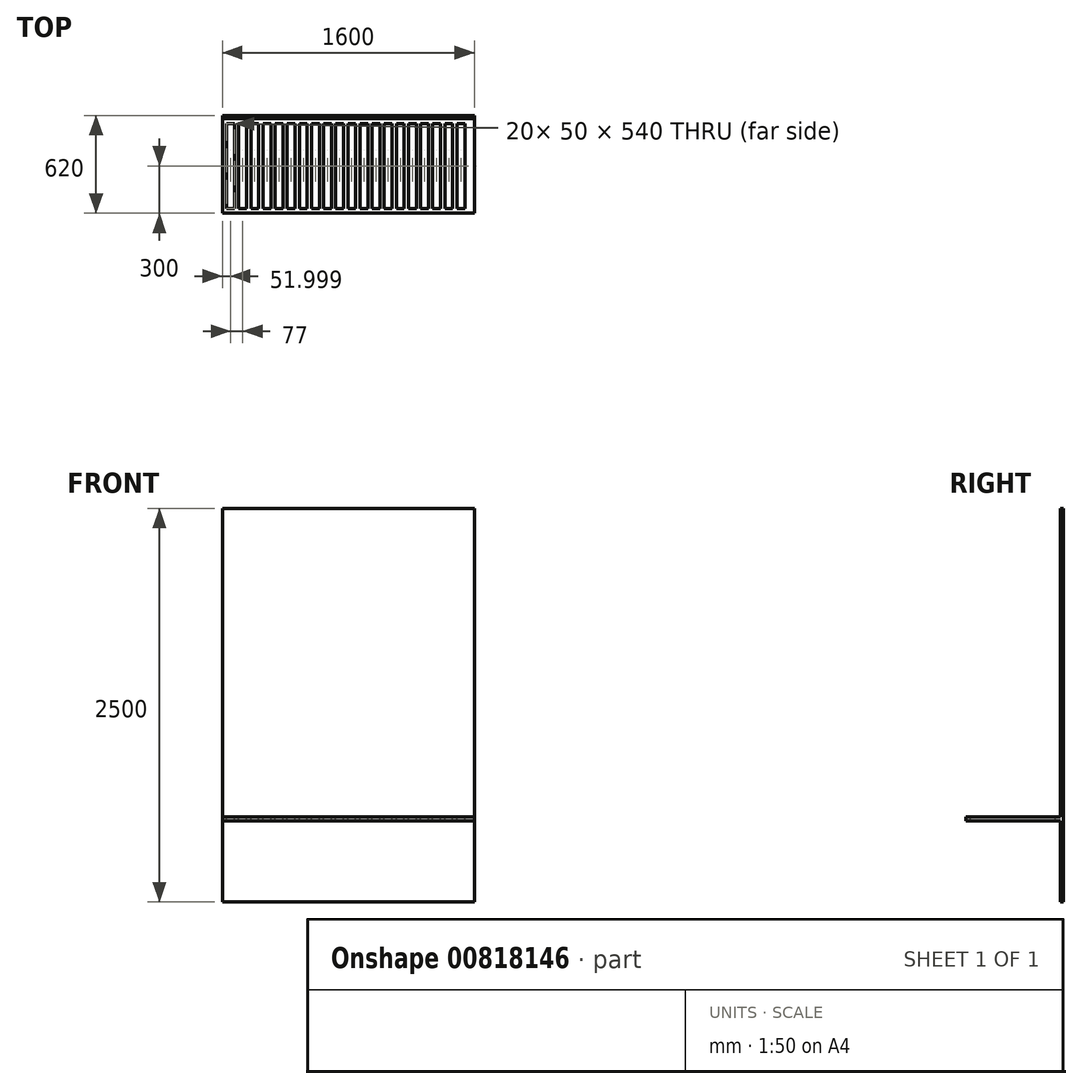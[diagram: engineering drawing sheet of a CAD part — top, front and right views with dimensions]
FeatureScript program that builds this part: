
annotation { "Feature Type Name" : "Feature", "Feature Type Description" : "" }
export const myFeature = defineFeature(function(context is Context, id is Id, definition is map)
    precondition{}
    {
        {
            var Q0;
            Q0=qCreatedBy(makeId("Front.planeOp"),FACE);
            var sketch = newSketch(context, id + "F0", { "sketchPlane" : qUnion([Q0])});
            skLineSegment(sketch, "E0.bottom", {"start": v(-816.96, 1960.36) * mm, "end": v(783.04, 1960.36) * mm});
            skLineSegment(sketch, "E0.top", {"start": v(-816.96, -539.64) * mm, "end": v(783.04, -539.64) * mm});
            skLineSegment(sketch, "E0.left", {"start": v(-816.96, 1960.36) * mm, "end": v(-816.96, -539.64) * mm});
            skLineSegment(sketch, "E0.right", {"start": v(783.04, 1960.36) * mm, "end": v(783.04, -539.64) * mm});
            skSolve(sketch);
        }
        {
            var Q0;
            Q0=makeQuery(id+"F0.imprint","IMPRINT",FACE,{"disambiguationData":[TD([[makeQuery(id+"F0.imprint","IMPRINT",EDGE,{"derivedFrom":sQuery(id+"F0.wireOp",EDGE,"E0.bottom")}),-1.0]])]});
            extrude(context, id + "F1", {"entities" : qUnion([Q0]), "depth" : 20 * mm, "offsetDistance" : 25 * mm});
        }
        {
            var Q0;
            Q0=makeQuery(id+"F1.opExtrude","CAP_FACE",FACE,{"disambiguationData":[OSD([sQuery(id+"F0.wireOp",EDGE,"E0.bottom"),sQuery(id+"F0.wireOp",EDGE,"E0.top"),sQuery(id+"F0.wireOp",EDGE,"E0.left"),sQuery(id+"F0.wireOp",EDGE,"E0.right")])],"isStart":false});
            var sketch = newSketch(context, id + "F2", { "sketchPlane" : qUnion([Q0])});
            skLineSegment(sketch, "E1.bottom", {"start": v(783.04, -25) * mm, "end": v(-816.96, -25) * mm});
            skLineSegment(sketch, "E1.top", {"start": v(783.04, 0) * mm, "end": v(-816.96, 0) * mm});
            skLineSegment(sketch, "E1.left", {"start": v(783.04, -25) * mm, "end": v(783.04, 0) * mm});
            skLineSegment(sketch, "E1.right", {"start": v(-816.96, -25) * mm, "end": v(-816.96, 0) * mm});
            skSolve(sketch);
        }
        {
            var Q0;
            Q0=makeQuery(id+"F2.imprint","IMPRINT",FACE,{"disambiguationData":[TD([[makeQuery(id+"F2.imprint","IMPRINT",EDGE,{"derivedFrom":sQuery(id+"F2.wireOp",EDGE,"E1.bottom")}),-1.0]])]});
            extrude(context, id + "F3", {"entities" : qUnion([Q0]), "operationType" : NewBodyOperationType.ADD, "depth" : 600 * mm, "offsetDistance" : 25 * mm});
        }
        {
            var Q0;
            Q0=makeQuery(id+"F3.opExtrude","SWEPT_FACE",FACE,{"disambiguationData":[OSD([sQuery(id+"F2.wireOp",EDGE,"E1.top")])]});
            var sketch = newSketch(context, id + "F4", { "sketchPlane" : qUnion([Q0])});
            skLineSegment(sketch, "E2.bottom", {"start": v(723.04, -590) * mm, "end": v(673.04, -590) * mm});
            skLineSegment(sketch, "E2.top", {"start": v(723.04, -50) * mm, "end": v(673.04, -50) * mm});
            skLineSegment(sketch, "E2.left", {"start": v(723.04, -590) * mm, "end": v(723.04, -50) * mm});
            skLineSegment(sketch, "E2.right", {"start": v(673.04, -590) * mm, "end": v(673.04, -50) * mm});
            skLineSegment(sketch, "E3.1.0.0", {"start": v(646.04, -50) * mm, "end": v(596.04, -50) * mm});
            skLineSegment(sketch, "E3.1.0.1", {"start": v(646.04, -590) * mm, "end": v(646.04, -50) * mm});
            skLineSegment(sketch, "E3.1.0.2", {"start": v(596.04, -590) * mm, "end": v(596.04, -50) * mm});
            skLineSegment(sketch, "E3.1.0.3", {"start": v(646.04, -590) * mm, "end": v(596.04, -590) * mm});
            skLineSegment(sketch, "E3.2.0.0", {"start": v(569.04, -50) * mm, "end": v(519.04, -50) * mm});
            skLineSegment(sketch, "E3.2.0.1", {"start": v(569.04, -590) * mm, "end": v(569.04, -50) * mm});
            skLineSegment(sketch, "E3.2.0.2", {"start": v(519.04, -590) * mm, "end": v(519.04, -50) * mm});
            skLineSegment(sketch, "E3.2.0.3", {"start": v(569.04, -590) * mm, "end": v(519.04, -590) * mm});
            skLineSegment(sketch, "E3.3.0.0", {"start": v(492.04, -50) * mm, "end": v(442.04, -50) * mm});
            skLineSegment(sketch, "E3.3.0.1", {"start": v(492.04, -590) * mm, "end": v(492.04, -50) * mm});
            skLineSegment(sketch, "E3.3.0.2", {"start": v(442.04, -590) * mm, "end": v(442.04, -50) * mm});
            skLineSegment(sketch, "E3.3.0.3", {"start": v(492.04, -590) * mm, "end": v(442.04, -590) * mm});
            skLineSegment(sketch, "E3.4.0.0", {"start": v(415.04, -50) * mm, "end": v(365.04, -50) * mm});
            skLineSegment(sketch, "E3.4.0.1", {"start": v(415.04, -590) * mm, "end": v(415.04, -50) * mm});
            skLineSegment(sketch, "E3.4.0.2", {"start": v(365.04, -590) * mm, "end": v(365.04, -50) * mm});
            skLineSegment(sketch, "E3.4.0.3", {"start": v(415.04, -590) * mm, "end": v(365.04, -590) * mm});
            skLineSegment(sketch, "E3.5.0.0", {"start": v(338.04, -50) * mm, "end": v(288.04, -50) * mm});
            skLineSegment(sketch, "E3.5.0.1", {"start": v(338.04, -590) * mm, "end": v(338.04, -50) * mm});
            skLineSegment(sketch, "E3.5.0.2", {"start": v(288.04, -590) * mm, "end": v(288.04, -50) * mm});
            skLineSegment(sketch, "E3.5.0.3", {"start": v(338.04, -590) * mm, "end": v(288.04, -590) * mm});
            skLineSegment(sketch, "E3.6.0.0", {"start": v(261.04, -50) * mm, "end": v(211.04, -50) * mm});
            skLineSegment(sketch, "E3.6.0.1", {"start": v(261.04, -590) * mm, "end": v(261.04, -50) * mm});
            skLineSegment(sketch, "E3.6.0.2", {"start": v(211.04, -590) * mm, "end": v(211.04, -50) * mm});
            skLineSegment(sketch, "E3.6.0.3", {"start": v(261.04, -590) * mm, "end": v(211.04, -590) * mm});
            skLineSegment(sketch, "E3.7.0.0", {"start": v(184.04, -50) * mm, "end": v(134.04, -50) * mm});
            skLineSegment(sketch, "E3.7.0.1", {"start": v(184.04, -590) * mm, "end": v(184.04, -50) * mm});
            skLineSegment(sketch, "E3.7.0.2", {"start": v(134.04, -590) * mm, "end": v(134.04, -50) * mm});
            skLineSegment(sketch, "E3.7.0.3", {"start": v(184.04, -590) * mm, "end": v(134.04, -590) * mm});
            skLineSegment(sketch, "E3.8.0.0", {"start": v(107.04, -50) * mm, "end": v(57.04, -50) * mm});
            skLineSegment(sketch, "E3.8.0.1", {"start": v(107.04, -590) * mm, "end": v(107.04, -50) * mm});
            skLineSegment(sketch, "E3.8.0.2", {"start": v(57.04, -590) * mm, "end": v(57.04, -50) * mm});
            skLineSegment(sketch, "E3.8.0.3", {"start": v(107.04, -590) * mm, "end": v(57.04, -590) * mm});
            skLineSegment(sketch, "E3.9.0.0", {"start": v(30.04, -50) * mm, "end": v(-19.96, -50) * mm});
            skLineSegment(sketch, "E3.9.0.1", {"start": v(30.04, -590) * mm, "end": v(30.04, -50) * mm});
            skLineSegment(sketch, "E3.9.0.2", {"start": v(-19.96, -590) * mm, "end": v(-19.96, -50) * mm});
            skLineSegment(sketch, "E3.9.0.3", {"start": v(30.04, -590) * mm, "end": v(-19.96, -590) * mm});
            skLineSegment(sketch, "E3.10.0.0", {"start": v(-46.96, -50) * mm, "end": v(-96.96, -50) * mm});
            skLineSegment(sketch, "E3.10.0.1", {"start": v(-46.96, -590) * mm, "end": v(-46.96, -50) * mm});
            skLineSegment(sketch, "E3.10.0.2", {"start": v(-96.96, -590) * mm, "end": v(-96.96, -50) * mm});
            skLineSegment(sketch, "E3.10.0.3", {"start": v(-46.96, -590) * mm, "end": v(-96.96, -590) * mm});
            skLineSegment(sketch, "E3.11.0.0", {"start": v(-123.96, -50) * mm, "end": v(-173.96, -50) * mm});
            skLineSegment(sketch, "E3.11.0.1", {"start": v(-123.96, -590) * mm, "end": v(-123.96, -50) * mm});
            skLineSegment(sketch, "E3.11.0.2", {"start": v(-173.96, -590) * mm, "end": v(-173.96, -50) * mm});
            skLineSegment(sketch, "E3.11.0.3", {"start": v(-123.96, -590) * mm, "end": v(-173.96, -590) * mm});
            skLineSegment(sketch, "E3.12.0.0", {"start": v(-200.96, -50) * mm, "end": v(-250.96, -50) * mm});
            skLineSegment(sketch, "E3.12.0.1", {"start": v(-200.96, -590) * mm, "end": v(-200.96, -50) * mm});
            skLineSegment(sketch, "E3.12.0.2", {"start": v(-250.96, -590) * mm, "end": v(-250.96, -50) * mm});
            skLineSegment(sketch, "E3.12.0.3", {"start": v(-200.96, -590) * mm, "end": v(-250.96, -590) * mm});
            skLineSegment(sketch, "E3.13.0.0", {"start": v(-277.96, -50) * mm, "end": v(-327.96, -50) * mm});
            skLineSegment(sketch, "E3.13.0.1", {"start": v(-277.96, -590) * mm, "end": v(-277.96, -50) * mm});
            skLineSegment(sketch, "E3.13.0.2", {"start": v(-327.96, -590) * mm, "end": v(-327.96, -50) * mm});
            skLineSegment(sketch, "E3.13.0.3", {"start": v(-277.96, -590) * mm, "end": v(-327.96, -590) * mm});
            skLineSegment(sketch, "E3.14.0.0", {"start": v(-354.96, -50) * mm, "end": v(-404.96, -50) * mm});
            skLineSegment(sketch, "E3.14.0.1", {"start": v(-354.96, -590) * mm, "end": v(-354.96, -50) * mm});
            skLineSegment(sketch, "E3.14.0.2", {"start": v(-404.96, -590) * mm, "end": v(-404.96, -50) * mm});
            skLineSegment(sketch, "E3.14.0.3", {"start": v(-354.96, -590) * mm, "end": v(-404.96, -590) * mm});
            skLineSegment(sketch, "E3.15.0.0", {"start": v(-431.96, -50) * mm, "end": v(-481.96, -50) * mm});
            skLineSegment(sketch, "E3.15.0.1", {"start": v(-431.96, -590) * mm, "end": v(-431.96, -50) * mm});
            skLineSegment(sketch, "E3.15.0.2", {"start": v(-481.96, -590) * mm, "end": v(-481.96, -50) * mm});
            skLineSegment(sketch, "E3.15.0.3", {"start": v(-431.96, -590) * mm, "end": v(-481.96, -590) * mm});
            skLineSegment(sketch, "E3.16.0.0", {"start": v(-508.96, -50) * mm, "end": v(-558.96, -50) * mm});
            skLineSegment(sketch, "E3.16.0.1", {"start": v(-508.96, -590) * mm, "end": v(-508.96, -50) * mm});
            skLineSegment(sketch, "E3.16.0.2", {"start": v(-558.96, -590) * mm, "end": v(-558.96, -50) * mm});
            skLineSegment(sketch, "E3.16.0.3", {"start": v(-508.96, -590) * mm, "end": v(-558.96, -590) * mm});
            skLineSegment(sketch, "E3.17.0.0", {"start": v(-585.96, -50) * mm, "end": v(-635.96, -50) * mm});
            skLineSegment(sketch, "E3.17.0.1", {"start": v(-585.96, -590) * mm, "end": v(-585.96, -50) * mm});
            skLineSegment(sketch, "E3.17.0.2", {"start": v(-635.96, -590) * mm, "end": v(-635.96, -50) * mm});
            skLineSegment(sketch, "E3.17.0.3", {"start": v(-585.96, -590) * mm, "end": v(-635.96, -590) * mm});
            skLineSegment(sketch, "E3.18.0.0", {"start": v(-662.96, -50) * mm, "end": v(-712.96, -50) * mm});
            skLineSegment(sketch, "E3.18.0.1", {"start": v(-662.96, -590) * mm, "end": v(-662.96, -50) * mm});
            skLineSegment(sketch, "E3.18.0.2", {"start": v(-712.96, -590) * mm, "end": v(-712.96, -50) * mm});
            skLineSegment(sketch, "E3.18.0.3", {"start": v(-662.96, -590) * mm, "end": v(-712.96, -590) * mm});
            skLineSegment(sketch, "E3.19.0.0", {"start": v(-739.96, -50) * mm, "end": v(-789.96, -50) * mm});
            skLineSegment(sketch, "E3.19.0.1", {"start": v(-739.96, -590) * mm, "end": v(-739.96, -50) * mm});
            skLineSegment(sketch, "E3.19.0.2", {"start": v(-789.96, -590) * mm, "end": v(-789.96, -50) * mm});
            skLineSegment(sketch, "E3.19.0.3", {"start": v(-739.96, -590) * mm, "end": v(-789.96, -590) * mm});
            skLineSegment(sketch, "E3.direction1", {"start": v(673.04, -590) * mm, "end": v(596.04, -590) * mm, "construction": true});
            skSolve(sketch);
        }
        {
            var Q0;
            Q0=makeQuery(id+"F4.imprint","IMPRINT",FACE,{"disambiguationData":[TD([[makeQuery(id+"F4.imprint","IMPRINT",EDGE,{"derivedFrom":sQuery(id+"F4.wireOp",EDGE,"E3.16.0.0")}),1.0]])]});
            var Q1;
            Q1=makeQuery(id+"F4.imprint","IMPRINT",FACE,{"disambiguationData":[TD([[makeQuery(id+"F4.imprint","IMPRINT",EDGE,{"derivedFrom":sQuery(id+"F4.wireOp",EDGE,"E3.17.0.0")}),1.0]])]});
            var Q2;
            Q2=makeQuery(id+"F4.imprint","IMPRINT",FACE,{"disambiguationData":[TD([[makeQuery(id+"F4.imprint","IMPRINT",EDGE,{"derivedFrom":sQuery(id+"F4.wireOp",EDGE,"E3.18.0.0")}),1.0]])]});
            var Q3;
            Q3=makeQuery(id+"F4.imprint","IMPRINT",FACE,{"disambiguationData":[TD([[makeQuery(id+"F4.imprint","IMPRINT",EDGE,{"derivedFrom":sQuery(id+"F4.wireOp",EDGE,"E3.19.0.0")}),1.0]])]});
            var Q4;
            Q4=makeQuery(id+"F4.imprint","IMPRINT",FACE,{"disambiguationData":[TD([[makeQuery(id+"F4.imprint","IMPRINT",EDGE,{"derivedFrom":sQuery(id+"F4.wireOp",EDGE,"E3.15.0.0")}),1.0]])]});
            var Q5;
            Q5=makeQuery(id+"F4.imprint","IMPRINT",FACE,{"disambiguationData":[TD([[makeQuery(id+"F4.imprint","IMPRINT",EDGE,{"derivedFrom":sQuery(id+"F4.wireOp",EDGE,"E3.13.0.0")}),1.0]])]});
            var Q6;
            Q6=makeQuery(id+"F4.imprint","IMPRINT",FACE,{"disambiguationData":[TD([[makeQuery(id+"F4.imprint","IMPRINT",EDGE,{"derivedFrom":sQuery(id+"F4.wireOp",EDGE,"E3.14.0.0")}),1.0]])]});
            var Q7;
            Q7=makeQuery(id+"F4.imprint","IMPRINT",FACE,{"disambiguationData":[TD([[makeQuery(id+"F4.imprint","IMPRINT",EDGE,{"derivedFrom":sQuery(id+"F4.wireOp",EDGE,"E2.bottom")}),-1.0]])]});
            var Q8;
            Q8=makeQuery(id+"F4.imprint","IMPRINT",FACE,{"disambiguationData":[TD([[makeQuery(id+"F4.imprint","IMPRINT",EDGE,{"derivedFrom":sQuery(id+"F4.wireOp",EDGE,"E3.1.0.0")}),1.0]])]});
            var Q9;
            Q9=makeQuery(id+"F4.imprint","IMPRINT",FACE,{"disambiguationData":[TD([[makeQuery(id+"F4.imprint","IMPRINT",EDGE,{"derivedFrom":sQuery(id+"F4.wireOp",EDGE,"E3.2.0.0")}),1.0]])]});
            var Q10;
            Q10=makeQuery(id+"F4.imprint","IMPRINT",FACE,{"disambiguationData":[TD([[makeQuery(id+"F4.imprint","IMPRINT",EDGE,{"derivedFrom":sQuery(id+"F4.wireOp",EDGE,"E3.3.0.0")}),1.0]])]});
            var Q11;
            Q11=makeQuery(id+"F4.imprint","IMPRINT",FACE,{"disambiguationData":[TD([[makeQuery(id+"F4.imprint","IMPRINT",EDGE,{"derivedFrom":sQuery(id+"F4.wireOp",EDGE,"E3.4.0.0")}),1.0]])]});
            var Q12;
            Q12=makeQuery(id+"F4.imprint","IMPRINT",FACE,{"disambiguationData":[TD([[makeQuery(id+"F4.imprint","IMPRINT",EDGE,{"derivedFrom":sQuery(id+"F4.wireOp",EDGE,"E3.5.0.0")}),1.0]])]});
            var Q13;
            Q13=makeQuery(id+"F4.imprint","IMPRINT",FACE,{"disambiguationData":[TD([[makeQuery(id+"F4.imprint","IMPRINT",EDGE,{"derivedFrom":sQuery(id+"F4.wireOp",EDGE,"E3.6.0.0")}),1.0]])]});
            var Q14;
            Q14=makeQuery(id+"F4.imprint","IMPRINT",FACE,{"disambiguationData":[TD([[makeQuery(id+"F4.imprint","IMPRINT",EDGE,{"derivedFrom":sQuery(id+"F4.wireOp",EDGE,"E3.7.0.0")}),1.0]])]});
            var Q15;
            Q15=makeQuery(id+"F4.imprint","IMPRINT",FACE,{"disambiguationData":[TD([[makeQuery(id+"F4.imprint","IMPRINT",EDGE,{"derivedFrom":sQuery(id+"F4.wireOp",EDGE,"E3.8.0.0")}),1.0]])]});
            var Q16;
            Q16=makeQuery(id+"F4.imprint","IMPRINT",FACE,{"disambiguationData":[TD([[makeQuery(id+"F4.imprint","IMPRINT",EDGE,{"derivedFrom":sQuery(id+"F4.wireOp",EDGE,"E3.9.0.0")}),1.0]])]});
            var Q17;
            Q17=makeQuery(id+"F4.imprint","IMPRINT",FACE,{"disambiguationData":[TD([[makeQuery(id+"F4.imprint","IMPRINT",EDGE,{"derivedFrom":sQuery(id+"F4.wireOp",EDGE,"E3.10.0.0")}),1.0]])]});
            var Q18;
            Q18=makeQuery(id+"F4.imprint","IMPRINT",FACE,{"disambiguationData":[TD([[makeQuery(id+"F4.imprint","IMPRINT",EDGE,{"derivedFrom":sQuery(id+"F4.wireOp",EDGE,"E3.11.0.0")}),1.0]])]});
            var Q19;
            Q19=makeQuery(id+"F4.imprint","IMPRINT",FACE,{"disambiguationData":[TD([[makeQuery(id+"F4.imprint","IMPRINT",EDGE,{"derivedFrom":sQuery(id+"F4.wireOp",EDGE,"E3.12.0.0")}),1.0]])]});
            var Q20;
            Q20=sQuery(id+"F4.wireOp",EDGE,"E3.19.0.2");
            var Q21;
            Q21=sQuery(id+"F4.wireOp",EDGE,"E3.19.0.1");
            var Q22;
            Q22=sQuery(id+"F4.wireOp",EDGE,"E3.19.0.3");
            var Q23;
            Q23=sQuery(id+"F4.wireOp",EDGE,"E3.19.0.0");
            extrude(context, id + "F5", {"entities" : qUnion([Q0, Q1, Q2, Q3, Q4, Q5, Q6, Q7, Q8, Q9, Q10, Q11, Q12, Q13, Q14, Q15, Q16, Q17, Q18, Q19]), "operationType" : NewBodyOperationType.REMOVE, "surfaceEntities" : qUnion([Q20, Q21, Q22, Q23]), "oppositeDirection" : true, "depth" : 216 * mm, "offsetDistance" : 25 * mm});
        }
    });
